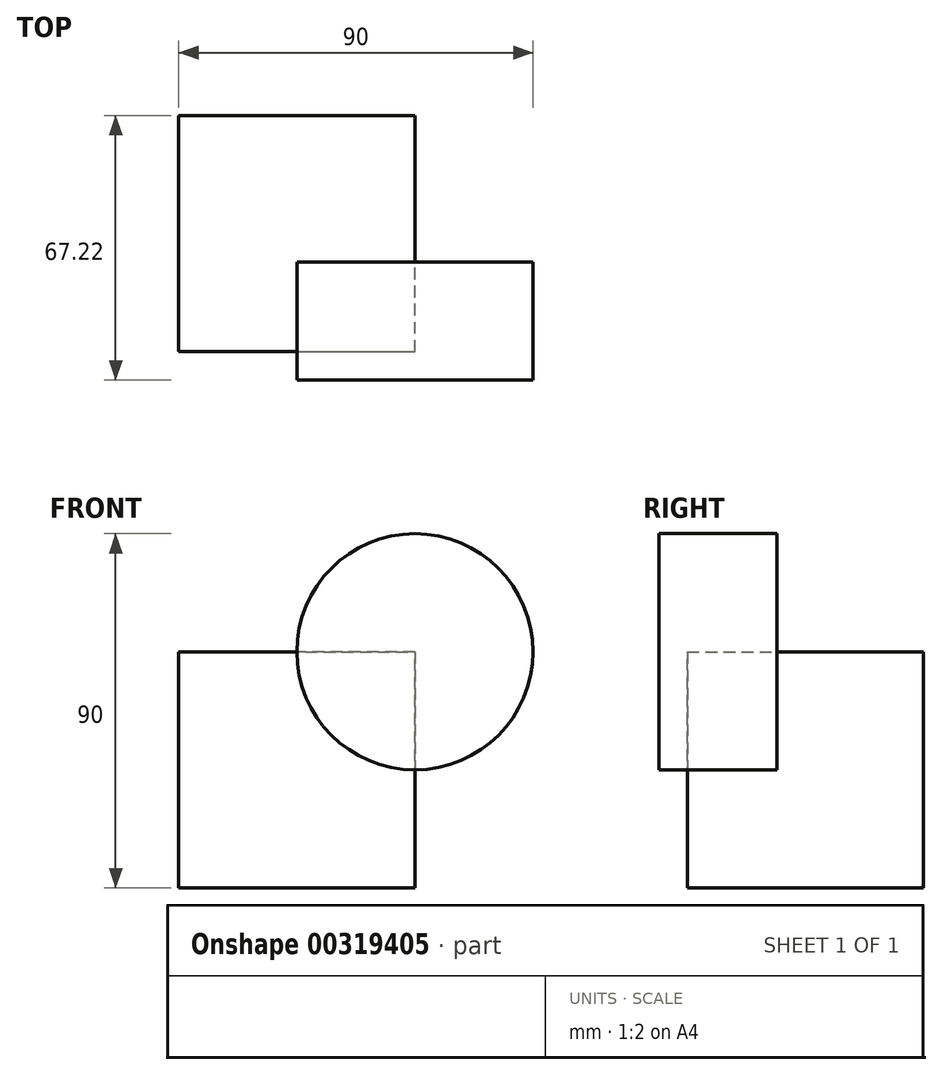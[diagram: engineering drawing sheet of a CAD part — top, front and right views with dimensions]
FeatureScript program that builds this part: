
annotation { "Feature Type Name" : "Feature", "Feature Type Description" : "" }
export const myFeature = defineFeature(function(context is Context, id is Id, definition is map)
    precondition{}
    {
        {
            var Q0;
            Q0=qCreatedBy(makeId("Front.planeOp"),FACE);
            var sketch = newSketch(context, id + "F0", { "sketchPlane" : qUnion([Q0])});
            skLineSegment(sketch, "E0.bottom", {"start": v(0, 0) * mm, "end": v(60, 0) * mm});
            skLineSegment(sketch, "E0.top", {"start": v(0, 60) * mm, "end": v(60, 60) * mm});
            skLineSegment(sketch, "E0.left", {"start": v(0, 0) * mm, "end": v(0, 60) * mm});
            skLineSegment(sketch, "E0.right", {"start": v(60, 0) * mm, "end": v(60, 60) * mm});
            skSolve(sketch);
        }
        {
            var Q0;
            Q0 = qSketchRegion(id + "F0", true);
            extrude(context, id + "F1", {"entities" : qUnion([Q0]), "depth" : 60 * mm});
        }
        {
            var Q0;
            Q0=makeQuery(id+"F1.opExtrude","SWEPT_FACE",FACE,{"disambiguationData":[OSD([sQuery(id+"F0.wireOp",EDGE,"E0.top")])]});
            var sketch = newSketch(context, id + "F2", { "sketchPlane" : qUnion([Q0])});
            skLineSegment(sketch, "E1.bottom", {"start": v(60, -37.22) * mm, "end": v(90, -37.22) * mm});
            skLineSegment(sketch, "E1.top", {"start": v(60, -67.22) * mm, "end": v(90, -67.22) * mm});
            skLineSegment(sketch, "E1.left", {"start": v(60, -37.22) * mm, "end": v(60, -67.22) * mm});
            skLineSegment(sketch, "E1.right", {"start": v(90, -37.22) * mm, "end": v(90, -67.22) * mm});
            skSolve(sketch);
        }
        {
            var Q0;
            Q0 = qSketchRegion(id + "F2", true);
            var Q1;
            Q1=sQuery(id+"F2.wireOp",EDGE,"E1.left");
            revolve(context, id + "F3", {"operationType" : NewBodyOperationType.ADD, "entities" : qUnion([Q0]), "axis" : qUnion([Q1]), "revolveType" : RevolveType.FULL});
        }
    });
